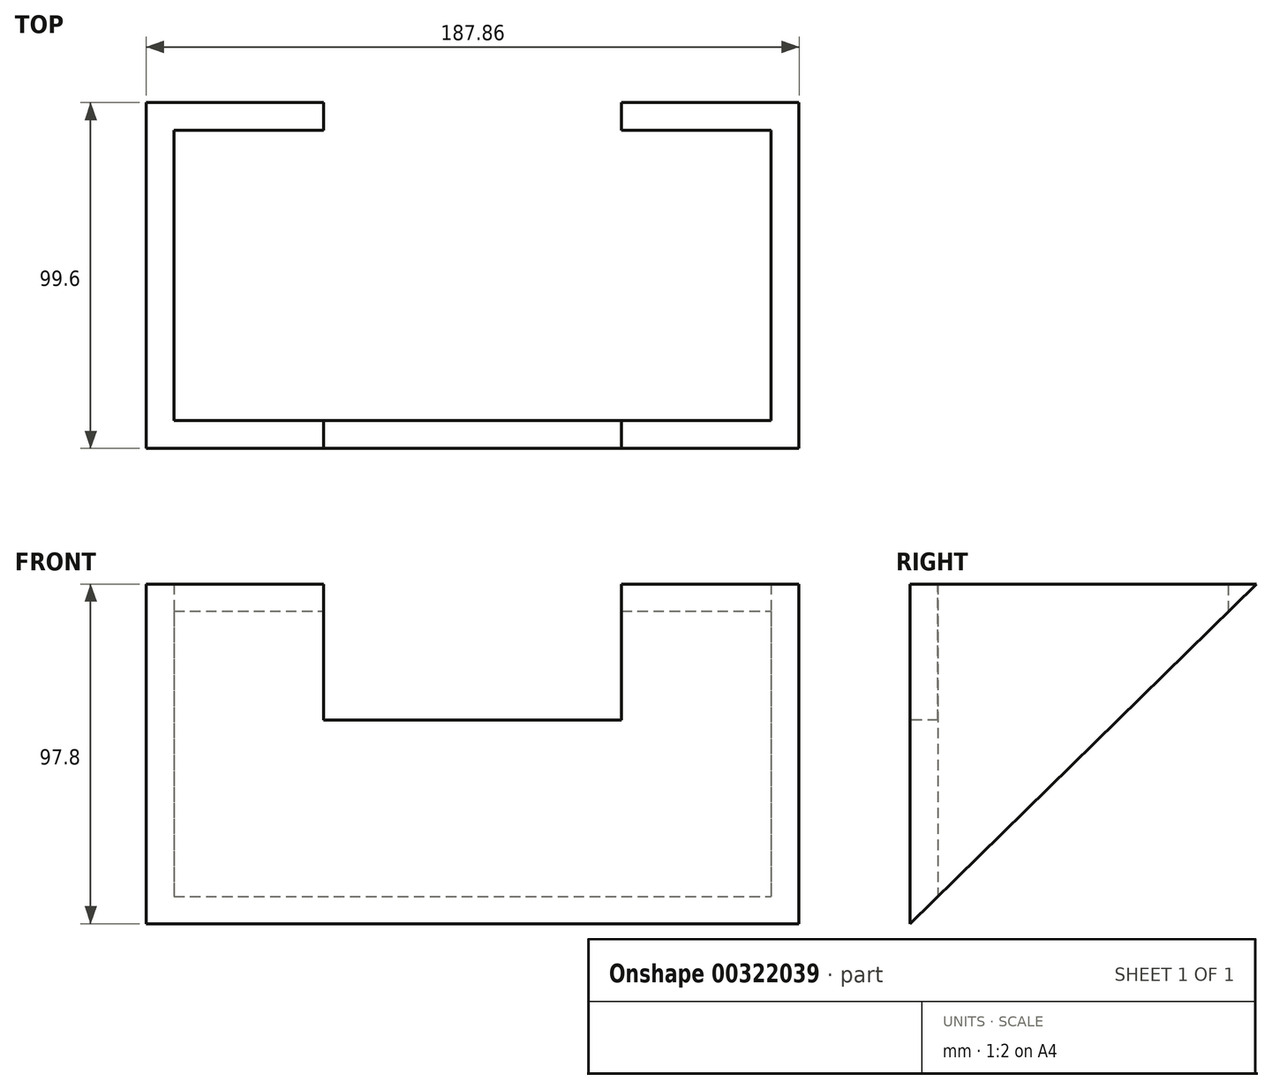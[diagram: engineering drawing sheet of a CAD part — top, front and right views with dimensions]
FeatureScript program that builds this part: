
annotation { "Feature Type Name" : "Feature", "Feature Type Description" : "" }
export const myFeature = defineFeature(function(context is Context, id is Id, definition is map)
    precondition{}
    {
        {
            var Q0;
            Q0=qCreatedBy(makeId("Top.planeOp"),FACE);
            var sketch = newSketch(context, id + "F0", { "sketchPlane" : qUnion([Q0])});
            skLineSegment(sketch, "E0.bottom", {"start": v(93.93, -49.8) * mm, "end": v(-93.93, -49.8) * mm});
            skLineSegment(sketch, "E0.top", {"start": v(93.93, 49.8) * mm, "end": v(-93.93, 49.8) * mm});
            skLineSegment(sketch, "E0.left", {"start": v(93.93, -49.8) * mm, "end": v(93.93, 49.8) * mm});
            skLineSegment(sketch, "E0.right", {"start": v(-93.93, -49.8) * mm, "end": v(-93.93, 49.8) * mm});
            skPoint(sketch, "E0.middle", {"position": v(0, 0) * mm});
            skLineSegment(sketch, "E1.0", {"start": v(85.93, 41.8) * mm, "end": v(-85.93, 41.8) * mm});
            skLineSegment(sketch, "E1.1", {"start": v(85.93, -41.8) * mm, "end": v(85.93, 41.8) * mm});
            skLineSegment(sketch, "E1.2", {"start": v(85.93, -41.8) * mm, "end": v(-85.93, -41.8) * mm});
            skLineSegment(sketch, "E1.3", {"start": v(-85.93, -41.8) * mm, "end": v(-85.93, 41.8) * mm});
            skSolve(sketch);
        }
        {
            var Q0;
            Q0=makeQuery(id+"F0.imprint","IMPRINT",FACE,{"disambiguationData":[TD([[makeQuery(id+"F0.imprint","IMPRINT",EDGE,{"derivedFrom":sQuery(id+"F0.wireOp",EDGE,"E0.bottom")}),-1.0]])]});
            extrude(context, id + "F1", {"entities" : qUnion([Q0]), "depth" : 97.8 * mm});
        }
        {
            var Q0;
            Q0=makeQuery(id+"F1.opExtrude","SWEPT_FACE",FACE,{"disambiguationData":[OSD([sQuery(id+"F0.wireOp",EDGE,"E0.left")])]});
            var sketch = newSketch(context, id + "F2", { "sketchPlane" : qUnion([Q0])});
            skLineSegment(sketch, "E2", {"start": v(-49.8, 97.8) * mm, "end": v(49.8, 0) * mm});
            skLineSegment(sketch, "E3", {"start": v(-49.8, 0) * mm, "end": v(49.8, 97.8) * mm});
            skCircle(sketch, "E4", {"center": v(0, 48.9) * mm, "radius": 11.3 * mm});
            skSolve(sketch);
        }
        {
            var Q0;
            {var subQ0=sQuery(id+"F2.wireOp",EDGE,"E4");var subQ1=sQuery(id+"F2.wireOp",EDGE,"E2");var subQ2=makeQuery(id+"F2.imprint","INTERSECT",VERTEX,{"disambiguationData":[OD(0.0)],"derivedFrom":[subQ1,subQ0]});Q0=makeQuery(id+"F2.imprint","IMPRINT",FACE,{"disambiguationData":[TD([[makeQuery(id+"F2.imprint","IMPRINT",EDGE,{"disambiguationData":[TD([[subQ2,-1.0]])],"derivedFrom":subQ1}),-1.0]])]});}
            var Q1;
            {var subQ0=sQuery(id+"F2.wireOp",EDGE,"E3");var subQ1=sQuery(id+"F2.wireOp",EDGE,"E2");var subQ2=makeQuery(id+"F2.imprint","INTERSECT",VERTEX,{"derivedFrom":[subQ1,subQ0]});Q1=makeQuery(id+"F2.imprint","IMPRINT",FACE,{"disambiguationData":[TD([[makeQuery(id+"F2.imprint","IMPRINT",EDGE,{"disambiguationData":[TD([[subQ2,-1.0]])],"derivedFrom":subQ1}),-1.0]])]});}
            var Q2;
            {var subQ0=sQuery(id+"F2.wireOp",EDGE,"E3");var subQ1=sQuery(id+"F2.wireOp",EDGE,"E2");var subQ2=makeQuery(id+"F2.imprint","INTERSECT",VERTEX,{"derivedFrom":[subQ1,subQ0]});Q2=makeQuery(id+"F2.imprint","IMPRINT",FACE,{"disambiguationData":[TD([[makeQuery(id+"F2.imprint","IMPRINT",EDGE,{"disambiguationData":[TD([[subQ2,-1.0]])],"derivedFrom":subQ1}),1.0]])]});}
            var Q3;
            {var subQ0=sQuery(id+"F2.wireOp",EDGE,"E4");var subQ1=sQuery(id+"F2.wireOp",EDGE,"E2");var subQ2=makeQuery(id+"F2.imprint","INTERSECT",VERTEX,{"disambiguationData":[OD(0.0)],"derivedFrom":[subQ1,subQ0]});Q3=makeQuery(id+"F2.imprint","IMPRINT",FACE,{"disambiguationData":[TD([[makeQuery(id+"F2.imprint","IMPRINT",EDGE,{"disambiguationData":[TD([[subQ2,-1.0]])],"derivedFrom":subQ1}),1.0]])]});}
            extrude(context, id + "F3", {"entities" : qUnion([Q0, Q1, Q2, Q3]), "operationType" : NewBodyOperationType.REMOVE, "endBound" : BoundingType.THROUGH_ALL, "oppositeDirection" : true, "depth" : 25 * mm});
        }
        {
            var Q0;
            Q0=makeQuery(id+"F1.opExtrude","SWEPT_FACE",FACE,{"disambiguationData":[OSD([sQuery(id+"F0.wireOp",EDGE,"E0.bottom")])]});
            var sketch = newSketch(context, id + "F4", { "sketchPlane" : qUnion([Q0])});
            skLineSegment(sketch, "E5.bottom", {"start": v(42.85, 58.64) * mm, "end": v(-42.85, 58.64) * mm});
            skLineSegment(sketch, "E5.top", {"start": v(42.85, 136.96) * mm, "end": v(-42.85, 136.96) * mm});
            skLineSegment(sketch, "E5.left", {"start": v(42.85, 58.64) * mm, "end": v(42.85, 136.96) * mm});
            skLineSegment(sketch, "E5.right", {"start": v(-42.85, 58.64) * mm, "end": v(-42.85, 136.96) * mm});
            skPoint(sketch, "E5.middle", {"position": v(0, 97.8) * mm});
            skSolve(sketch);
        }
        {
            var Q0;
            {var subQ0=sQuery(id+"F4.wireOp",EDGE,"E5.bottom");Q0=makeQuery(id+"F4.imprint","IMPRINT",FACE,{"disambiguationData":[TD([[makeQuery(id+"F4.imprint","IMPRINT",EDGE,{"derivedFrom":subQ0}),-1.0]])]});}
            extrude(context, id + "F5", {"entities" : qUnion([Q0]), "operationType" : NewBodyOperationType.REMOVE, "endBound" : BoundingType.THROUGH_ALL, "oppositeDirection" : true, "depth" : 25 * mm});
        }
    });
